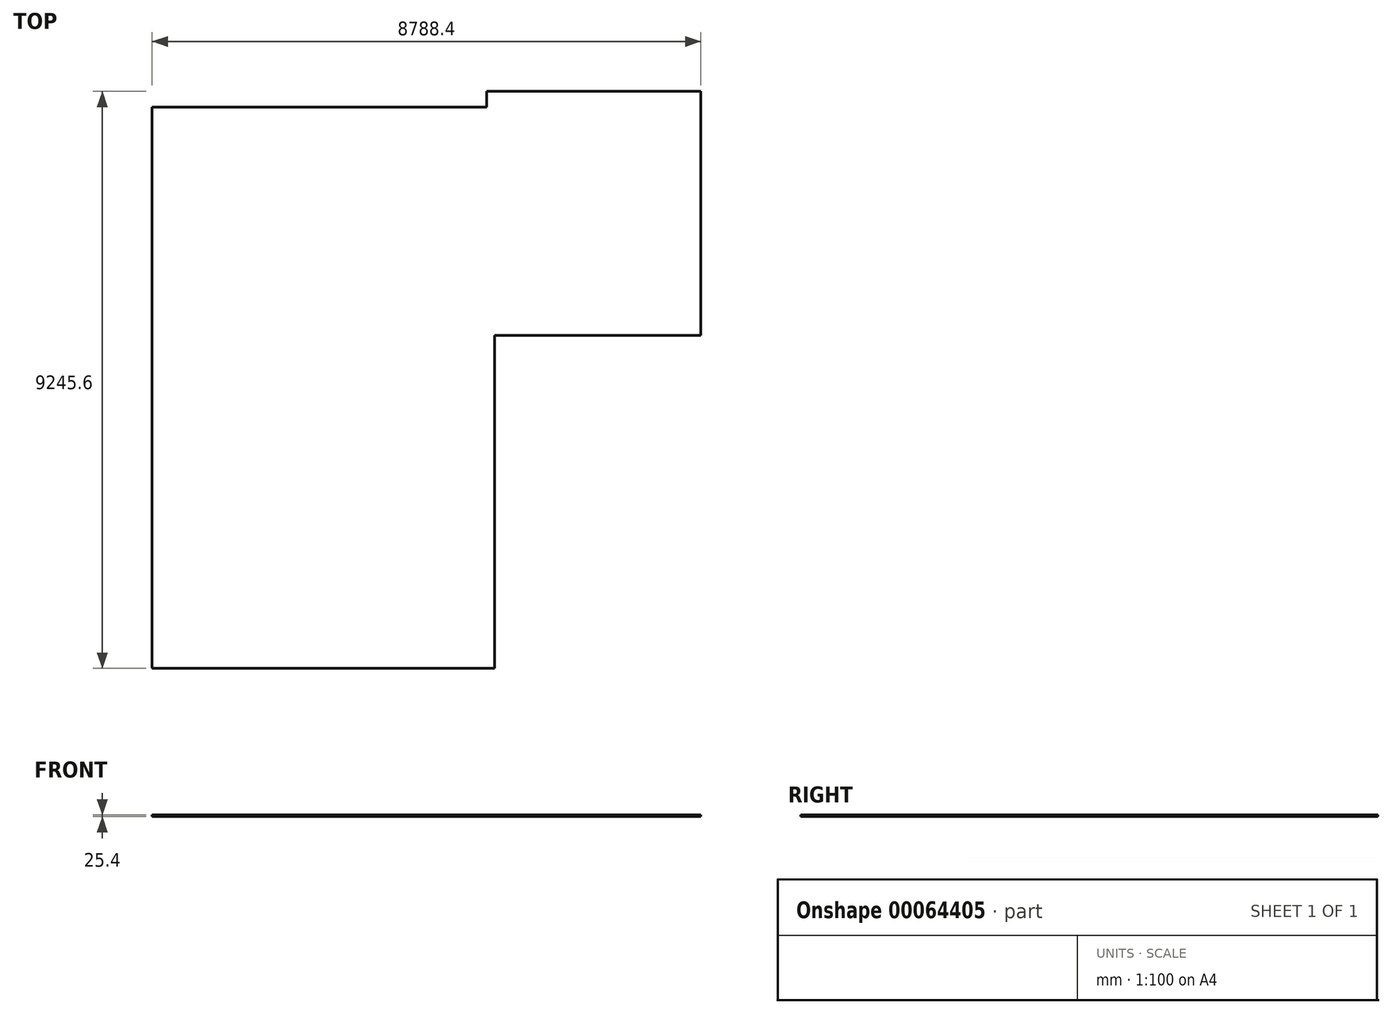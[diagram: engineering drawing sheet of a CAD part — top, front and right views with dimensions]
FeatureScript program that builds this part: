
annotation { "Feature Type Name" : "Feature", "Feature Type Description" : "" }
export const myFeature = defineFeature(function(context is Context, id is Id, definition is map)
    precondition{}
    {
        {
            var Q0;
            Q0=qCreatedBy(makeId("Top.planeOp"),FACE);
            var sketch = newSketch(context, id + "F0", { "sketchPlane" : qUnion([Q0])});
            skLineSegment(sketch, "E0.rect.bottom", {"start": v(-4394.2, 4495.8) * mm, "end": v(4394.2, 4495.8) * mm});
            skLineSegment(sketch, "E0.rect.top", {"start": v(-4394.2, -4495.8) * mm, "end": v(4394.2, -4495.8) * mm});
            skLineSegment(sketch, "E0.rect.left", {"start": v(-4394.2, 4495.8) * mm, "end": v(-4394.2, -4495.8) * mm});
            skLineSegment(sketch, "E0.rect.right", {"start": v(4394.2, 4495.8) * mm, "end": v(4394.2, -4495.8) * mm});
            skPoint(sketch, "E0.rect.middle", {"position": v(0, 0) * mm});
            skLineSegment(sketch, "E1", {"start": v(1092.2, -4495.8) * mm, "end": v(1092.2, 838.2) * mm});
            skLineSegment(sketch, "E2", {"start": v(1092.2, 838.2) * mm, "end": v(4394.2, 838.2) * mm});
            skLineSegment(sketch, "E3", {"start": v(965.2, 4749.8) * mm, "end": v(4394.2, 4749.8) * mm});
            skLineSegment(sketch, "E4", {"start": v(965.2, 4749.8) * mm, "end": v(965.2, 4495.8) * mm});
            skLineSegment(sketch, "E5", {"start": v(4394.2, 4749.8) * mm, "end": v(4394.2, 4495.8) * mm});
            skSolve(sketch);
        }
        {
            var Q0;
            Q0=makeQuery(id+"F0.imprint","IMPRINT",FACE,{"disambiguationData":[TD([[makeQuery(id+"F0.imprint","IMPRINT",EDGE,{"derivedFrom":sQuery(id+"F0.wireOp",EDGE,"E3")}),-1.0]])]});
            var Q1;
            {var subQ0=sQuery(id+"F0.wireOp",EDGE,"E0.rect.left");Q1=makeQuery(id+"F0.imprint","IMPRINT",FACE,{"disambiguationData":[TD([[makeQuery(id+"F0.imprint","IMPRINT",EDGE,{"derivedFrom":subQ0}),1.0]])]});}
            extrude(context, id + "F1", {"entities" : qUnion([Q0, Q1]), "depth" : 25.4 * mm});
        }
    });
